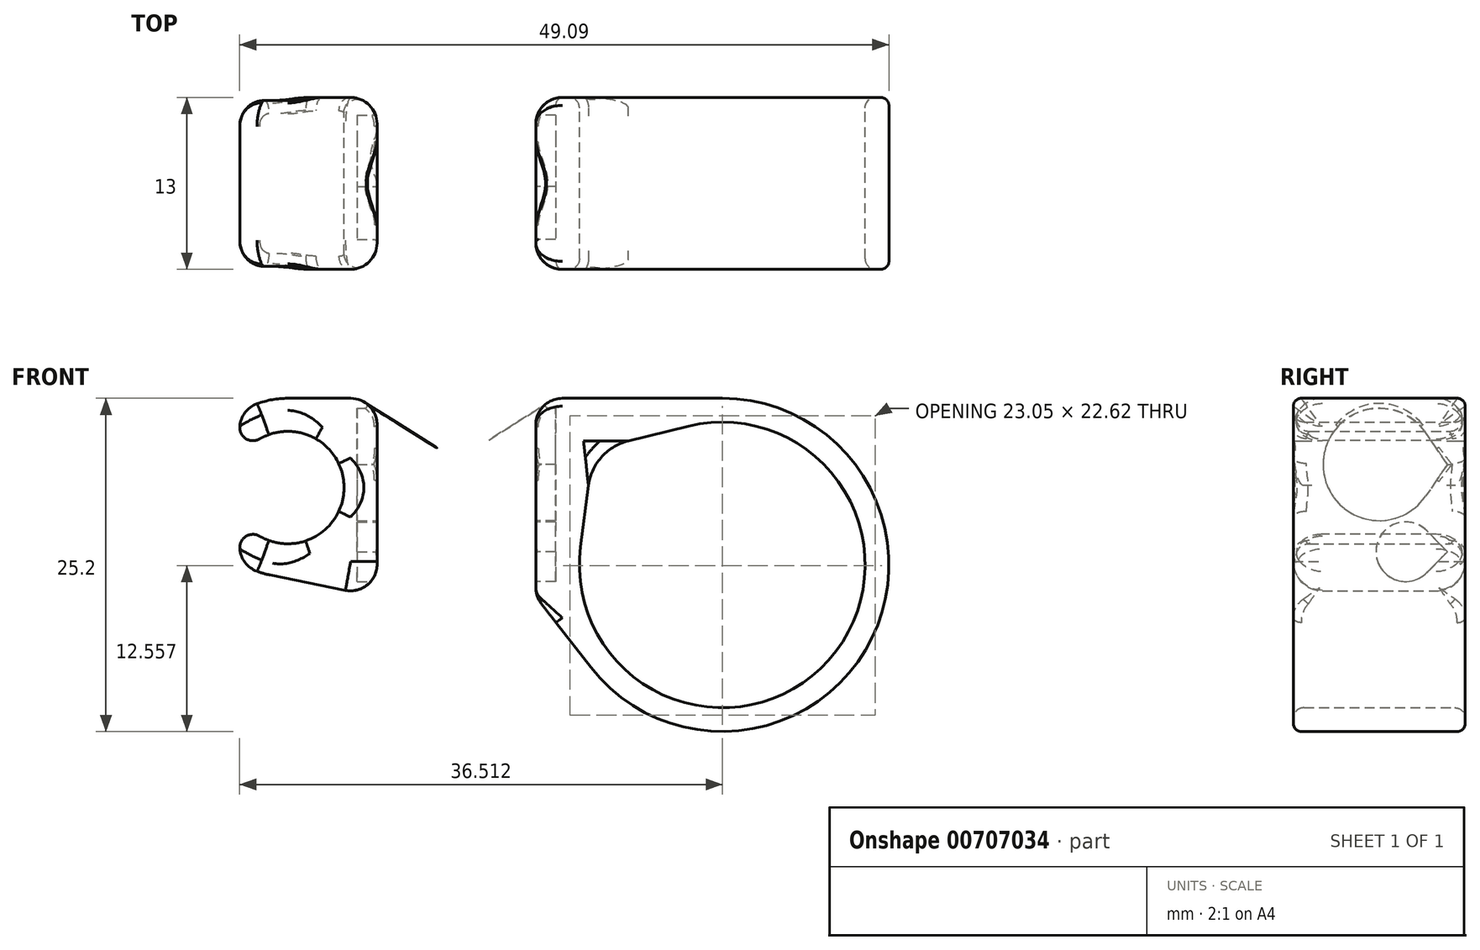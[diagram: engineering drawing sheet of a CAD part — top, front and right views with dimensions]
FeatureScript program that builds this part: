
annotation { "Feature Type Name" : "Feature", "Feature Type Description" : "" }
export const myFeature = defineFeature(function(context is Context, id is Id, definition is map)
    precondition{}
    {
        {
            var Q0;
            Q0=qCreatedBy(makeId("Front.planeOp"),FACE);
            var sketch = newSketch(context, id + "F0", { "sketchPlane" : qUnion([Q0])});
            skCircle(sketch, "E0", {"center": v(0, 0) * mm, "radius": 10.8 * mm});
            skCircle(sketch, "E1", {"center": v(0, 0) * mm, "radius": 12.6 * mm});
            skLineSegment(sketch, "E2", {"start": v(0, 12.6) * mm, "end": v(-14.1, 12.6) * mm});
            skLineSegment(sketch, "E3", {"start": v(10.8, 0) * mm, "end": v(12.6, 0) * mm, "construction": true});
            skLineSegment(sketch, "E4", {"start": v(-14.1, -2.4) * mm, "end": v(-9.94, -7.74) * mm});
            skCircle(sketch, "E5", {"center": v(-32.85, 5.85) * mm, "radius": 4.25 * mm});
            skCircle(sketch, "E6", {"center": v(-32.85, 5.85) * mm, "radius": 6.75 * mm});
            skLineSegment(sketch, "E7", {"start": v(-32.85, 12.6) * mm, "end": v(-26.1, 12.6) * mm});
            skLineSegment(sketch, "E8", {"start": v(-26.1, -2.4) * mm, "end": v(-34.19, -0.77) * mm});
            skLineSegment(sketch, "E9", {"start": v(-14.1, 12.6) * mm, "end": v(-14.1, -2.4) * mm});
            skLineSegment(sketch, "E10", {"start": v(-26.1, 12.6) * mm, "end": v(-26.1, -2.4) * mm});
            skLineSegment(sketch, "E11", {"start": v(-26.1, 12.6) * mm, "end": v(-14.1, 12.6) * mm, "construction": true});
            skLineSegment(sketch, "E12", {"start": v(-37.63, 10.61) * mm, "end": v(-35.86, 8.85) * mm});
            skLineSegment(sketch, "E13", {"start": v(-35.86, 2.85) * mm, "end": v(-37.63, 1.09) * mm});
            skLineSegment(sketch, "E14", {"start": v(-35.86, 8.85) * mm, "end": v(-35.86, 2.85) * mm, "construction": true});
            skLineSegment(sketch, "E15", {"start": v(-12.6, 0) * mm, "end": v(-14.1, 0) * mm, "construction": true});
            skLineSegment(sketch, "E16", {"start": v(-14.1, 12.6) * mm, "end": v(-9.77, 8.73) * mm, "construction": true});
            skLineSegment(sketch, "E17", {"start": v(-9.77, 8.73) * mm, "end": v(-9.4, 8.4) * mm, "construction": true});
            skLineSegment(sketch, "E18", {"start": v(-9.77, 8.73) * mm, "end": v(-10.89, 0) * mm});
            skLineSegment(sketch, "E19", {"start": v(-9.77, 8.73) * mm, "end": v(-2.57, 10.5) * mm});
            skSolve(sketch);
        }
        {
            var Q0;
            {var subQ0=sQuery(id+"F0.wireOp",EDGE,"E2");Q0=makeQuery(id+"F0.imprint","IMPRINT",FACE,{"disambiguationData":[TD([[makeQuery(id+"F0.imprint","IMPRINT",EDGE,{"derivedFrom":subQ0}),1.0]])]});}
            var Q1;
            {var subQ0=sQuery(id+"F0.wireOp",EDGE,"BOMHUTUy-HUa9-tjrQ-onbM-w2NflRtOryE0");Q1=makeQuery(id+"F0.imprint","IMPRINT",FACE,{"disambiguationData":[TD([[makeQuery(id+"F0.imprint","IMPRINT",EDGE,{"derivedFrom":subQ0}),1.0]])]});}
            var Q2;
            {var subQ0=sQuery(id+"F0.wireOp",EDGE,"E4");Q2=makeQuery(id+"F0.imprint","IMPRINT",FACE,{"disambiguationData":[TD([[makeQuery(id+"F0.imprint","IMPRINT",EDGE,{"derivedFrom":subQ0}),1.0]])]});}
            var Q3;
            {var subQ0=sQuery(id+"F0.wireOp",EDGE,"E7");Q3=makeQuery(id+"F0.imprint","IMPRINT",FACE,{"disambiguationData":[TD([[makeQuery(id+"F0.imprint","IMPRINT",EDGE,{"derivedFrom":subQ0}),-1.0]])]});}
            var Q4;
            {var subQ0=sQuery(id+"F0.wireOp",EDGE,"E8");Q4=makeQuery(id+"F0.imprint","IMPRINT",FACE,{"disambiguationData":[TD([[makeQuery(id+"F0.imprint","IMPRINT",EDGE,{"derivedFrom":subQ0}),-1.0]])]});}
            var Q5;
            {var subQ5=sQuery(id+"F0.wireOp",EDGE,"E12");Q5=makeQuery(id+"F0.imprint","IMPRINT",FACE,{"disambiguationData":[TD([[makeQuery(id+"F0.imprint","IMPRINT",EDGE,{"derivedFrom":subQ5}),1.0]])]});}
            var Q6;
            {var subQ5=sQuery(id+"F0.wireOp",EDGE,"E19");var subQ7=sQuery(id+"F0.wireOp",EDGE,"E0");var subQ8=makeQuery(id+"F0.imprint","INTERSECT",VERTEX,{"derivedFrom":[subQ7,subQ5]});Q6=makeQuery(id+"F0.imprint","IMPRINT",FACE,{"disambiguationData":[TD([[makeQuery(id+"F0.imprint","IMPRINT",EDGE,{"disambiguationData":[TD([[subQ8,1.0]])],"derivedFrom":subQ7}),-1.0]])]});}
            extrude(context, id + "F1", {"entities" : qUnion([Q0, Q1, Q2, Q3, Q4, Q5, Q6]), "depth" : 13 * mm, "offsetDistance" : 25 * mm});
        }
        {
            var Q0;
            Q0=makeQuery(id+"F1.opExtrude","SWEPT_FACE",FACE,{"disambiguationData":[OSD([sQuery(id+"F0.wireOp",EDGE,"E9")])]});
            var sketch = newSketch(context, id + "F2", { "sketchPlane" : qUnion([Q0])});
            skCircle(sketch, "E20", {"center": v(6.5, 7.6) * mm, "radius": 4.25 * mm});
            skCircle(sketch, "E21", {"center": v(4.5, 1) * mm, "radius": 2.25 * mm});
            skLineSegment(sketch, "E22", {"start": v(6.5, 7.6) * mm, "end": v(6.5, 12.6) * mm, "construction": true});
            skLineSegment(sketch, "E23", {"start": v(2.25, 7.6) * mm, "end": v(2.25, 1) * mm, "construction": true});
            skLineSegment(sketch, "E24", {"start": v(5.15, 3.15) * mm, "end": v(5.27, 3.53) * mm, "construction": true});
            skLineSegment(sketch, "E25.0", {"start": v(13, 12.6) * mm, "end": v(0, 12.6) * mm, "construction": true});
            skLineSegment(sketch, "E26", {"start": v(1.35, 7.6) * mm, "end": v(3, 10) * mm});
            skLineSegment(sketch, "E27", {"start": v(1.35, 7.6) * mm, "end": v(3, 5.2) * mm});
            skLineSegment(sketch, "E28", {"start": v(1.35, 7.6) * mm, "end": v(2.25, 7.6) * mm, "construction": true});
            skLineSegment(sketch, "E29", {"start": v(2.25, 1) * mm, "end": v(1.35, 1) * mm, "construction": true});
            skLineSegment(sketch, "E30", {"start": v(1.35, 1) * mm, "end": v(2.9, 2.57) * mm});
            skLineSegment(sketch, "E31", {"start": v(1.35, 1) * mm, "end": v(2.9, -0.58) * mm});
            skSolve(sketch);
        }
        {
            var Q0;
            Q0=makeQuery(id+"F1.opExtrude","SWEPT_FACE",FACE,{"disambiguationData":[OSD([sQuery(id+"F0.wireOp",EDGE,"E10")])]});
            var sketch = newSketch(context, id + "F3", { "sketchPlane" : qUnion([Q0])});
            skCircle(sketch, "E32.0", {"center": v(-6.5, 7.6) * mm, "radius": 4.25 * mm});
            skCircle(sketch, "E33.0", {"center": v(-4.5, 1) * mm, "radius": 2.25 * mm});
            skLineSegment(sketch, "E34.0", {"start": v(-1.35, 7.6) * mm, "end": v(-3, 10) * mm});
            skLineSegment(sketch, "E35.0", {"start": v(-1.35, 7.6) * mm, "end": v(-3, 5.2) * mm});
            skLineSegment(sketch, "E36.0", {"start": v(-1.35, 1) * mm, "end": v(-2.9, 2.57) * mm});
            skLineSegment(sketch, "E37.0", {"start": v(-1.35, 1) * mm, "end": v(-2.9, -0.58) * mm});
            skSolve(sketch);
        }
        {
            var Q0;
            Q0 = qSketchRegion(id + "F2", true);
            extrude(context, id + "F4", {"entities" : qUnion([Q0]), "operationType" : NewBodyOperationType.REMOVE, "oppositeDirection" : true, "depth" : 1.5 * mm, "offsetDistance" : 25 * mm});
        }
        {
            var Q0;
            Q0 = qSketchRegion(id + "F3", true);
            extrude(context, id + "F5", {"entities" : qUnion([Q0]), "operationType" : NewBodyOperationType.REMOVE, "oppositeDirection" : true, "depth" : 1.5 * mm, "offsetDistance" : 25 * mm});
        }
        {
            var Q0;
            Q0=makeQuery(id+"F1.opExtrude","SWEPT_EDGE",EDGE,{"disambiguationData":[OSD([sQuery(id+"F0.wireOp",EDGE,"E2"),sQuery(id+"F0.wireOp",EDGE,"E9")])]});
            var Q1;
            Q1=makeQuery(id+"F1.opExtrude","CAP_EDGE",EDGE,{"disambiguationData":[OSD([sQuery(id+"F0.wireOp",EDGE,"E9")])],"isStart":true});
            var Q2;
            Q2=makeQuery(id+"F1.opExtrude","SWEPT_EDGE",EDGE,{"disambiguationData":[OSD([sQuery(id+"F0.wireOp",EDGE,"E4"),sQuery(id+"F0.wireOp",EDGE,"E9")])]});
            var Q3;
            Q3=makeQuery(id+"F1.opExtrude","CAP_EDGE",EDGE,{"disambiguationData":[OSD([sQuery(id+"F0.wireOp",EDGE,"E9")])],"isStart":false});
            var Q4;
            Q4=makeQuery(id+"F1.opExtrude","SWEPT_EDGE",EDGE,{"disambiguationData":[OSD([sQuery(id+"F0.wireOp",EDGE,"E8"),sQuery(id+"F0.wireOp",EDGE,"E10")])]});
            var Q5;
            Q5=makeQuery(id+"F1.opExtrude","CAP_EDGE",EDGE,{"disambiguationData":[OSD([sQuery(id+"F0.wireOp",EDGE,"E10")])],"isStart":false});
            var Q6;
            Q6=makeQuery(id+"F1.opExtrude","SWEPT_EDGE",EDGE,{"disambiguationData":[OSD([sQuery(id+"F0.wireOp",EDGE,"E7"),sQuery(id+"F0.wireOp",EDGE,"E10")])]});
            var Q7;
            Q7=makeQuery(id+"F1.opExtrude","CAP_EDGE",EDGE,{"disambiguationData":[OSD([sQuery(id+"F0.wireOp",EDGE,"E10")])],"isStart":true});
            fillet(context, id + "F6", {"entities" : qUnion([Q0, Q1, Q2, Q3, Q4, Q5, Q6, Q7]), "radius" : 2 * mm, "allowEdgeOverflow" : false});
        }
        {
            var Q0;
            {var subQ0=sQuery(id+"F0.wireOp",EDGE,"E10");Q0=makeQuery(id+"F6.opFillet","BLEND_EDGE",EDGE,{"blendedFrom":[makeQuery(id+"F1.opExtrude","SWEPT_EDGE",EDGE,{"disambiguationData":[OSD([sQuery(id+"F0.wireOp",EDGE,"E8"),subQ0])]}),makeQuery(id+"F1.opExtrude","CAP_EDGE",EDGE,{"disambiguationData":[OSD([subQ0])],"isStart":false})],"blendedInto":[]});}
            var Q1;
            {var subQ0=sQuery(id+"F0.wireOp",EDGE,"E10");Q1=makeQuery(id+"F6.opFillet","BLEND_EDGE",EDGE,{"blendedFrom":[makeQuery(id+"F1.opExtrude","SWEPT_EDGE",EDGE,{"disambiguationData":[OSD([sQuery(id+"F0.wireOp",EDGE,"E8"),subQ0])]}),makeQuery(id+"F1.opExtrude","CAP_EDGE",EDGE,{"disambiguationData":[OSD([subQ0])],"isStart":true})],"blendedInto":[]});}
            var Q2;
            {var subQ0=sQuery(id+"F0.wireOp",EDGE,"E10");Q2=makeQuery(id+"F6.opFillet","BLEND_EDGE",EDGE,{"blendedFrom":[makeQuery(id+"F1.opExtrude","SWEPT_EDGE",EDGE,{"disambiguationData":[OSD([sQuery(id+"F0.wireOp",EDGE,"E7"),subQ0])]}),makeQuery(id+"F1.opExtrude","CAP_EDGE",EDGE,{"disambiguationData":[OSD([subQ0])],"isStart":false})],"blendedInto":[]});}
            var Q3;
            {var subQ0=sQuery(id+"F0.wireOp",EDGE,"E10");Q3=makeQuery(id+"F6.opFillet","BLEND_EDGE",EDGE,{"blendedFrom":[makeQuery(id+"F1.opExtrude","SWEPT_EDGE",EDGE,{"disambiguationData":[OSD([sQuery(id+"F0.wireOp",EDGE,"E7"),subQ0])]}),makeQuery(id+"F1.opExtrude","CAP_EDGE",EDGE,{"disambiguationData":[OSD([subQ0])],"isStart":true})],"blendedInto":[]});}
            fillet(context, id + "F7", {"entities" : qUnion([Q0, Q1, Q2, Q3]), "radius" : 2.2 * mm, "tangentPropagation" : true, "allowEdgeOverflow" : false});
        }
        {
            var Q0;
            Q0=makeQuery(id+"F1.opExtrude","SWEPT_EDGE",EDGE,{"disambiguationData":[OSD([sQuery(id+"F0.wireOp",EDGE,"E6"),sQuery(id+"F0.wireOp",EDGE,"E13")])]});
            var Q1;
            Q1=makeQuery(id+"F1.opExtrude","SWEPT_EDGE",EDGE,{"disambiguationData":[OSD([sQuery(id+"F0.wireOp",EDGE,"E6"),sQuery(id+"F0.wireOp",EDGE,"E12")])]});
            fillet(context, id + "F8", {"entities" : qUnion([Q0, Q1]), "radius" : 2 * mm, "tangentPropagation" : true, "allowEdgeOverflow" : false});
        }
        {
            var Q0;
            Q0=makeQuery(id+"F1.opExtrude","SWEPT_EDGE",EDGE,{"disambiguationData":[OSD([sQuery(id+"F0.wireOp",EDGE,"E5"),sQuery(id+"F0.wireOp",EDGE,"E12")])]});
            fillet(context, id + "F9", {"entities" : qUnion([Q0]), "radius" : 1 * mm, "tangentPropagation" : true, "allowEdgeOverflow" : false});
        }
        {
            var Q0;
            Q0=makeQuery(id+"F6.opFillet","BLEND_EDGE",EDGE,{"blendedFrom":[makeQuery(id+"F1.opExtrude","CAP_EDGE",EDGE,{"disambiguationData":[OSD([sQuery(id+"F0.wireOp",EDGE,"E10")])],"isStart":true}),makeQuery(id+"F5.boolean.opBoolean","COPY",FACE,{"derivedFrom":makeQuery(id+"F5.opExtrude","SWEPT_FACE",FACE,{"disambiguationData":[OSD([sQuery(id+"F3.wireOp",EDGE,"E35.0")])]})})],"blendedInto":[makeQuery(id+"F5.boolean.opBoolean","COPY",FACE,{"derivedFrom":makeQuery(id+"F5.opExtrude","SWEPT_FACE",FACE,{"disambiguationData":[OSD([sQuery(id+"F3.wireOp",EDGE,"E35.0")])]})})]});
            var Q1;
            Q1=makeQuery(id+"F5.boolean.opBoolean","COPY",EDGE,{"derivedFrom":makeQuery(id+"F5.opExtrude","CAP_EDGE",EDGE,{"disambiguationData":[OSD([sQuery(id+"F3.wireOp",EDGE,"E33.0")])],"isStart":true})});
            var Q2;
            Q2=makeQuery(id+"F6.opFillet","BLEND_EDGE",EDGE,{"blendedFrom":[makeQuery(id+"F1.opExtrude","SWEPT_EDGE",EDGE,{"disambiguationData":[OSD([sQuery(id+"F0.wireOp",EDGE,"E2"),sQuery(id+"F0.wireOp",EDGE,"E9")])]}),makeQuery(id+"F4.boolean.opBoolean","COPY",FACE,{"derivedFrom":makeQuery(id+"F4.opExtrude","SWEPT_FACE",FACE,{"disambiguationData":[OSD([sQuery(id+"F2.wireOp",EDGE,"E20")])]})})],"blendedInto":[makeQuery(id+"F4.boolean.opBoolean","COPY",FACE,{"derivedFrom":makeQuery(id+"F4.opExtrude","SWEPT_FACE",FACE,{"disambiguationData":[OSD([sQuery(id+"F2.wireOp",EDGE,"E20")])]})})]});
            fillet(context, id + "F10", {"entities" : qUnion([Q0, Q1, Q2]), "radius" : 0.2 * mm, "tangentPropagation" : true, "allowEdgeOverflow" : false});
        }
        {
            var Q0;
            {var subQ0=sQuery(id+"F0.wireOp",EDGE,"E9");Q0=makeQuery(id+"F6.opFillet","BLEND_EDGE",EDGE,{"blendedFrom":[makeQuery(id+"F1.opExtrude","SWEPT_EDGE",EDGE,{"disambiguationData":[OSD([sQuery(id+"F0.wireOp",EDGE,"E4"),subQ0])]}),makeQuery(id+"F1.opExtrude","CAP_EDGE",EDGE,{"disambiguationData":[OSD([subQ0])],"isStart":true})],"blendedInto":[]});}
            var Q1;
            {var subQ0=sQuery(id+"F0.wireOp",EDGE,"E9");Q1=makeQuery(id+"F6.opFillet","BLEND_EDGE",EDGE,{"blendedFrom":[makeQuery(id+"F1.opExtrude","SWEPT_EDGE",EDGE,{"disambiguationData":[OSD([sQuery(id+"F0.wireOp",EDGE,"E2"),subQ0])]}),makeQuery(id+"F1.opExtrude","CAP_EDGE",EDGE,{"disambiguationData":[OSD([subQ0])],"isStart":true})],"blendedInto":[]});}
            var Q2;
            {var subQ0=sQuery(id+"F0.wireOp",EDGE,"E9");Q2=makeQuery(id+"F6.opFillet","BLEND_EDGE",EDGE,{"blendedFrom":[makeQuery(id+"F1.opExtrude","SWEPT_EDGE",EDGE,{"disambiguationData":[OSD([sQuery(id+"F0.wireOp",EDGE,"E2"),subQ0])]}),makeQuery(id+"F1.opExtrude","CAP_EDGE",EDGE,{"disambiguationData":[OSD([subQ0])],"isStart":false})],"blendedInto":[]});}
            var Q3;
            {var subQ0=sQuery(id+"F0.wireOp",EDGE,"E9");Q3=makeQuery(id+"F6.opFillet","BLEND_EDGE",EDGE,{"blendedFrom":[makeQuery(id+"F1.opExtrude","SWEPT_EDGE",EDGE,{"disambiguationData":[OSD([sQuery(id+"F0.wireOp",EDGE,"E4"),subQ0])]}),makeQuery(id+"F1.opExtrude","CAP_EDGE",EDGE,{"disambiguationData":[OSD([subQ0])],"isStart":false})],"blendedInto":[]});}
            fillet(context, id + "F11", {"entities" : qUnion([Q0, Q1, Q2, Q3]), "radius" : 0.6 * mm, "tangentPropagation" : true, "allowEdgeOverflow" : false});
        }
        {
            var Q0;
            Q0=makeQuery(id+"F1.opExtrude","CAP_EDGE",EDGE,{"disambiguationData":[OSD([sQuery(id+"F0.wireOp",EDGE,"E0")])],"isStart":true});
            var Q1;
            Q1=makeQuery(id+"F1.opExtrude","CAP_EDGE",EDGE,{"disambiguationData":[OSD([sQuery(id+"F0.wireOp",EDGE,"E0")])],"isStart":false});
            fillet(context, id + "F12", {"entities" : qUnion([Q0, Q1]), "radius" : .8 * mm, "tangentPropagation" : true, "allowEdgeOverflow" : false});
        }
        {
            var Q0;
            Q0=makeQuery(id+"F1.opExtrude","SWEPT_EDGE",EDGE,{"disambiguationData":[OSD([sQuery(id+"F0.wireOp",EDGE,"E18"),sQuery(id+"F0.wireOp",EDGE,"E19")])]});
            fillet(context, id + "F13", {"entities" : qUnion([Q0]), "radius" : 4 * mm, "tangentPropagation" : true, "allowEdgeOverflow" : false});
        }
    });
